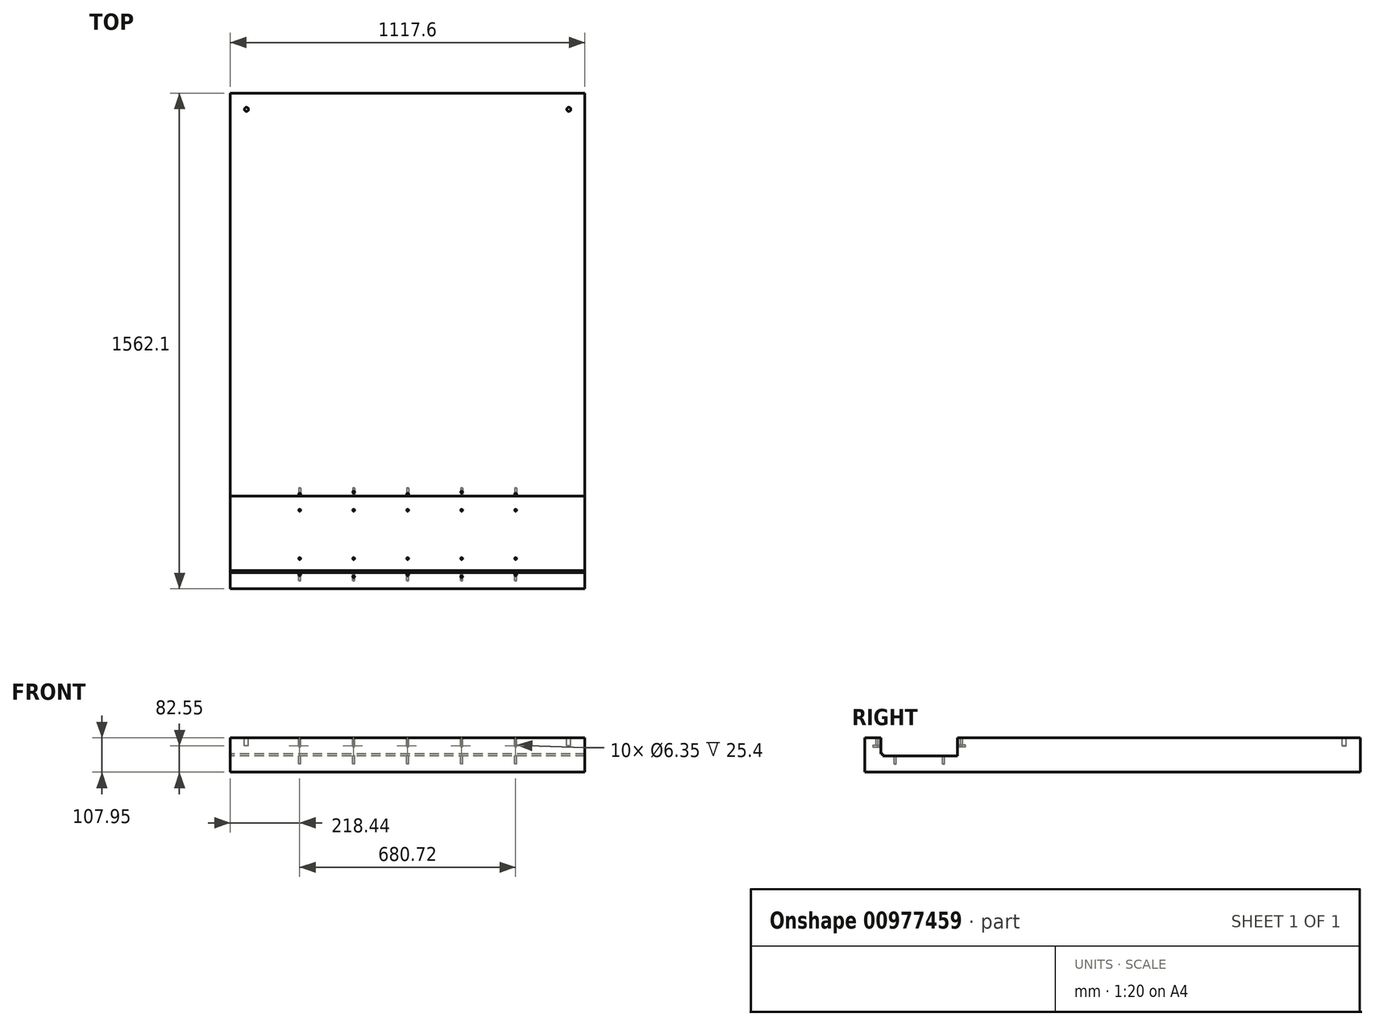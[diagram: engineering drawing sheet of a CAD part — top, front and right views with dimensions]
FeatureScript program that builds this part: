
annotation { "Feature Type Name" : "Feature", "Feature Type Description" : "" }
export const myFeature = defineFeature(function(context is Context, id is Id, definition is map)
    precondition{}
    {
        {
            var Q0;
            Q0=qCreatedBy(makeId("Right.planeOp"),FACE);
            var sketch = newSketch(context, id + "F0", { "sketchPlane" : qUnion([Q0])});
            skLineSegment(sketch, "E0", {"start": v(-171.45, 0) * mm, "end": v(1390.65, 0) * mm});
            skLineSegment(sketch, "E1", {"start": v(1390.65, 0) * mm, "end": v(1390.65, 107.95) * mm});
            skLineSegment(sketch, "E2", {"start": v(-171.45, 0) * mm, "end": v(-171.45, 107.95) * mm});
            skLineSegment(sketch, "E3", {"start": v(-171.45, 107.95) * mm, "end": v(-120.65, 107.95) * mm});
            skLineSegment(sketch, "E4", {"start": v(-120.65, 107.95) * mm, "end": v(-120.65, 50.8) * mm});
            skLineSegment(sketch, "E5", {"start": v(-120.65, 50.8) * mm, "end": v(120.65, 50.8) * mm});
            skLineSegment(sketch, "E6", {"start": v(120.65, 50.8) * mm, "end": v(120.65, 107.95) * mm});
            skLineSegment(sketch, "E7", {"start": v(120.65, 107.95) * mm, "end": v(1390.65, 107.95) * mm});
            skPoint(sketch, "E8", {"position": v(0, 50.8) * mm});
            skLineSegment(sketch, "E9.bottom", {"start": v(-120.65, 50.8) * mm, "end": v(-114.3, 50.8) * mm});
            skLineSegment(sketch, "E9.top", {"start": v(-120.65, 57.15) * mm, "end": v(-114.3, 57.15) * mm});
            skLineSegment(sketch, "E9.left", {"start": v(-120.65, 50.8) * mm, "end": v(-120.65, 57.15) * mm});
            skLineSegment(sketch, "E9.right", {"start": v(-114.3, 50.8) * mm, "end": v(-114.3, 57.15) * mm});
            skSolve(sketch);
        }
        {
            var Q0;
            Q0=qSketchRegion(id+"F0",true);
            extrude(context, id + "F1", {"entities" : qUnion([Q0]), "endBound" : BoundingType.SYMMETRIC, "depth" : 1117.6 * mm, "offsetDistance" : 25.4 * mm});
        }
        {
            var Q0;
            Q0=makeQuery(id+"F1.opExtrude","SWEPT_FACE",FACE,{"disambiguationData":[OSD([sQuery(id+"F0.wireOp",EDGE,"E5")])]});
            var sketch = newSketch(context, id + "F2", { "sketchPlane" : qUnion([Q0])});
            skCircle(sketch, "E10", {"center": v(170.18, -76.2) * mm, "radius": 3.18 * mm});
            skCircle(sketch, "E11", {"center": v(0, -76.2) * mm, "radius": 3.18 * mm});
            skCircle(sketch, "E12", {"center": v(-170.18, -76.2) * mm, "radius": 3.18 * mm});
            skCircle(sketch, "E13.MirrorC", {"center": v(0, 76.2) * mm, "radius": 3.18 * mm});
            skCircle(sketch, "E14.MirrorC", {"center": v(-170.18, 76.2) * mm, "radius": 3.18 * mm});
            skCircle(sketch, "E15.MirrorC", {"center": v(170.18, 76.2) * mm, "radius": 3.18 * mm});
            skCircle(sketch, "E16", {"center": v(-340.36, -76.2) * mm, "radius": 3.18 * mm});
            skCircle(sketch, "E17.MirrorC", {"center": v(340.36, -76.2) * mm, "radius": 3.18 * mm});
            skCircle(sketch, "E18.MirrorC", {"center": v(-340.36, 76.2) * mm, "radius": 3.18 * mm});
            skCircle(sketch, "E19.MirrorC", {"center": v(340.36, 76.2) * mm, "radius": 3.18 * mm});
            skSolve(sketch);
        }
        {
            var Q0;
            Q0=qSketchRegion(id+"F2",true);
            extrude(context, id + "F3", {"entities" : qUnion([Q0]), "operationType" : NewBodyOperationType.REMOVE, "oppositeDirection" : true, "depth" : 25.4 * mm, "offsetDistance" : 25.4 * mm});
        }
        {
            var Q0;
            Q0=makeQuery(id+"F1.opExtrude","SWEPT_FACE",FACE,{"disambiguationData":[OSD([sQuery(id+"F0.wireOp",EDGE,"E6")])]});
            var sketch = newSketch(context, id + "F4", { "sketchPlane" : qUnion([Q0])});
            skCircle(sketch, "E20", {"center": v(0, 82.55) * mm, "radius": 3.18 * mm});
            skCircle(sketch, "E21", {"center": v(-170.18, 82.55) * mm, "radius": 3.18 * mm});
            skCircle(sketch, "E22", {"center": v(-340.36, 82.55) * mm, "radius": 3.18 * mm});
            skCircle(sketch, "E23.MirrorC", {"center": v(170.18, 82.55) * mm, "radius": 3.18 * mm});
            skCircle(sketch, "E24.MirrorC", {"center": v(340.36, 82.55) * mm, "radius": 3.18 * mm});
            skSolve(sketch);
        }
        {
            var Q0;
            Q0=qSketchRegion(id+"F4",true);
            extrude(context, id + "F5", {"entities" : qUnion([Q0]), "operationType" : NewBodyOperationType.REMOVE, "oppositeDirection" : true, "depth" : 25.4 * mm, "offsetDistance" : 25.4 * mm});
        }
        {
            var Q0;
            Q0=makeQuery(id+"F1.opExtrude","SWEPT_FACE",FACE,{"disambiguationData":[OSD([sQuery(id+"F0.wireOp",EDGE,"E4")])]});
            var sketch = newSketch(context, id + "F6", { "sketchPlane" : qUnion([Q0])});
            skCircle(sketch, "E25", {"center": v(0, 82.55) * mm, "radius": 3.18 * mm});
            skCircle(sketch, "E26", {"center": v(-170.18, 82.55) * mm, "radius": 3.18 * mm});
            skCircle(sketch, "E27", {"center": v(-340.36, 82.55) * mm, "radius": 3.18 * mm});
            skCircle(sketch, "E28.MirrorC", {"center": v(170.18, 82.55) * mm, "radius": 3.18 * mm});
            skCircle(sketch, "E29.MirrorC", {"center": v(340.36, 82.55) * mm, "radius": 3.18 * mm});
            skSolve(sketch);
        }
        {
            var Q0;
            Q0=qSketchRegion(id+"F6",true);
            extrude(context, id + "F7", {"entities" : qUnion([Q0]), "operationType" : NewBodyOperationType.REMOVE, "oppositeDirection" : true, "depth" : 25.4 * mm, "offsetDistance" : 25.4 * mm});
        }
        {
            var Q0;
            Q0=makeQuery(id+"F1.opExtrude","SWEPT_FACE",FACE,{"disambiguationData":[OSD([sQuery(id+"F0.wireOp",EDGE,"E3")])]});
            var sketch = newSketch(context, id + "F8", { "sketchPlane" : qUnion([Q0])});
            skCircle(sketch, "E30", {"center": v(0, -127) * mm, "radius": 3.18 * mm});
            skPoint(sketch, "E30.centerSnap0", {"position": v(0, -120.65) * mm});
            skCircle(sketch, "E31", {"center": v(-340.36, -127) * mm, "radius": 3.18 * mm});
            skCircle(sketch, "E32", {"center": v(-170.18, -133.35) * mm, "radius": 3.17 * mm});
            skCircle(sketch, "E33.MirrorC", {"center": v(170.18, -133.35) * mm, "radius": 3.17 * mm});
            skCircle(sketch, "E34.MirrorC", {"center": v(340.36, -127) * mm, "radius": 3.18 * mm});
            skCircle(sketch, "E35.MirrorC", {"center": v(-340.36, 127) * mm, "radius": 3.18 * mm});
            skCircle(sketch, "E36.MirrorC", {"center": v(-170.18, 133.35) * mm, "radius": 3.17 * mm});
            skCircle(sketch, "E37.MirrorC", {"center": v(0, 127) * mm, "radius": 3.18 * mm});
            skCircle(sketch, "E38.MirrorC", {"center": v(170.18, 133.35) * mm, "radius": 3.17 * mm});
            skCircle(sketch, "E39.MirrorC", {"center": v(340.36, 127) * mm, "radius": 3.18 * mm});
            skSolve(sketch);
        }
        {
            var Q0;
            Q0=qSketchRegion(id+"F8",true);
            extrude(context, id + "F9", {"entities" : qUnion([Q0]), "operationType" : NewBodyOperationType.REMOVE, "oppositeDirection" : true, "depth" : 25.4 * mm, "offsetDistance" : 25.4 * mm});
        }
        {
            var Q0;
            Q0=makeQuery(id+"F1.opExtrude","SWEPT_FACE",FACE,{"disambiguationData":[OSD([sQuery(id+"F0.wireOp",EDGE,"E7")])]});
            var sketch = newSketch(context, id + "F10", { "sketchPlane" : qUnion([Q0])});
            skCircle(sketch, "E40", {"center": v(508, 1339.85) * mm, "radius": 6.35 * mm});
            skCircle(sketch, "E41", {"center": v(-508, 1339.85) * mm, "radius": 6.35 * mm});
            skSolve(sketch);
        }
        {
            var Q0;
            Q0 = qSketchRegion(id + "F10", true);
            extrude(context, id + "F11", {"entities" : qUnion([Q0]), "operationType" : NewBodyOperationType.REMOVE, "oppositeDirection" : true, "depth" : 25.4 * mm, "offsetDistance" : 25.4 * mm});
        }
    });
